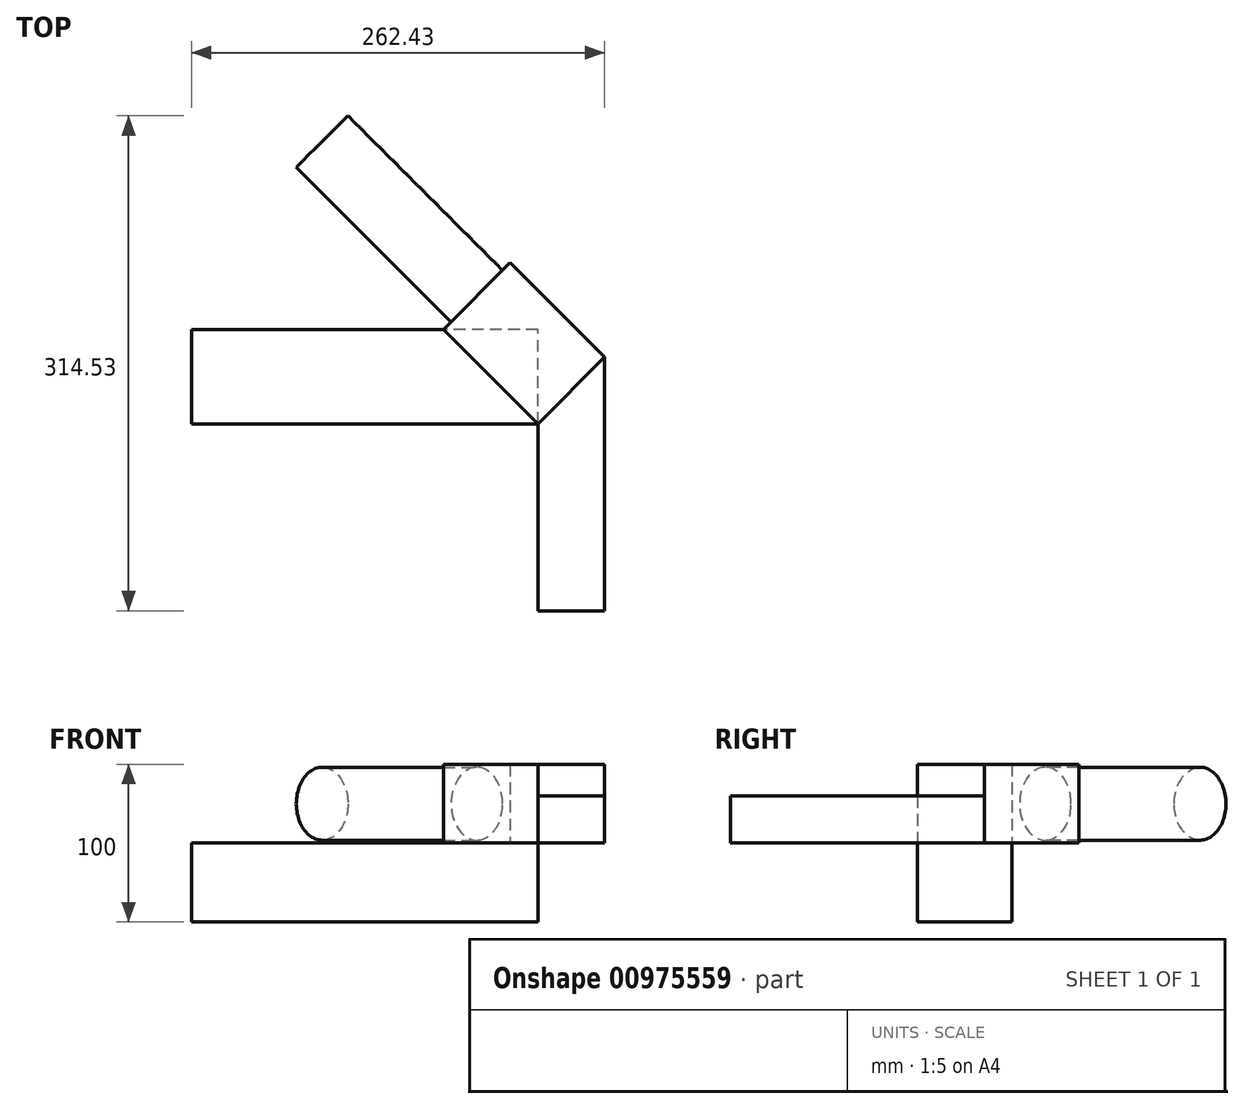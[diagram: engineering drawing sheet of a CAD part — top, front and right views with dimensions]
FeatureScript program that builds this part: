
annotation { "Feature Type Name" : "Feature", "Feature Type Description" : "" }
export const myFeature = defineFeature(function(context is Context, id is Id, definition is map)
    precondition{}
    {
        {
            var Q0;
            Q0=qCreatedBy(makeId("Top.planeOp"),FACE);
            var sketch = newSketch(context, id + "F0", { "sketchPlane" : qUnion([Q0])});
            skLineSegment(sketch, "E0.bottom", {"start": v(110, -30) * mm, "end": v(-110, -30) * mm});
            skLineSegment(sketch, "E0.top", {"start": v(110, 30) * mm, "end": v(-110, 30) * mm});
            skLineSegment(sketch, "E0.left", {"start": v(110, -30) * mm, "end": v(110, 30) * mm});
            skLineSegment(sketch, "E0.right", {"start": v(-110, -30) * mm, "end": v(-110, 30) * mm});
            skPoint(sketch, "E0.middle", {"position": v(0, 0) * mm});
            skSolve(sketch);
        }
        {
            var Q0;
            Q0 = qSketchRegion(id + "F0", true);
            extrude(context, id + "F1", {"entities" : qUnion([Q0]), "depth" : 50 * mm, "offsetDistance" : 25 * mm});
        }
        {
            var Q0;
            Q0=makeQuery(id+"F1.opExtrude","CAP_FACE",FACE,{"disambiguationData":[OSD([sQuery(id+"F0.wireOp",EDGE,"E0.bottom"),sQuery(id+"F0.wireOp",EDGE,"E0.top"),sQuery(id+"F0.wireOp",EDGE,"E0.left"),sQuery(id+"F0.wireOp",EDGE,"E0.right")])],"isStart":false});
            var sketch = newSketch(context, id + "F2", { "sketchPlane" : qUnion([Q0])});
            skLineSegment(sketch, "E1", {"start": v(110, -30) * mm, "end": v(50, 30) * mm});
            skLineSegment(sketch, "E2", {"start": v(110, -30) * mm, "end": v(152.43, 12.43) * mm});
            skLineSegment(sketch, "E3", {"start": v(152.43, 12.43) * mm, "end": v(92.43, 72.43) * mm});
            skLineSegment(sketch, "E4", {"start": v(92.43, 72.43) * mm, "end": v(50, 30) * mm});
            skSolve(sketch);
        }
        {
            var Q0;
            Q0 = qSketchRegion(id + "F2", true);
            extrude(context, id + "F3", {"entities" : qUnion([Q0]), "operationType" : NewBodyOperationType.ADD, "depth" : 50 * mm, "offsetDistance" : 25 * mm});
        }
        {
            var Q0;
            Q0 = qSketchRegion(id + "F2", true);
            extrude(context, id + "F4", {"entities" : qUnion([Q0]), "operationType" : NewBodyOperationType.ADD, "depth" : 25 * mm, "offsetDistance" : 25 * mm});
        }
        {
            var Q0;
            Q0=makeQuery(id+"F3.opExtrude","SWEPT_FACE",FACE,{"disambiguationData":[OSD([sQuery(id+"F2.wireOp",EDGE,"E4")])]});
            var sketch = newSketch(context, id + "F5", { "sketchPlane" : qUnion([Q0])});
            skPoint(sketch, "E5", {"position": v(-86.57, 75) * mm});
            skCircle(sketch, "E6", {"center": v(-86.57, 75) * mm, "radius": 20 * mm});
            skSolve(sketch);
        }
        {
            var Q0;
            Q0 = qSketchRegion(id + "F5", true);
            extrude(context, id + "F6", {"entities" : qUnion([Q0]), "operationType" : NewBodyOperationType.REMOVE, "oppositeDirection" : true, "depth" : 60 * mm, "offsetDistance" : 25 * mm, "hasDraft" : true, "draftAngle" : 3 * degree});
        }
        {
            var Q0;
            Q0=makeQuery(id+"F6.boolean.opBoolean","COPY",FACE,{"derivedFrom":makeQuery(id+"F6.opExtrude","CAP_FACE",FACE,{"disambiguationData":[OSD([sQuery(id+"F5.wireOp",EDGE,"E6")])],"isStart":false})});
            extrude(context, id + "F7", {"entities" : qUnion([Q0]), "operationType" : NewBodyOperationType.ADD, "depth" : 199 * mm, "offsetDistance" : 25 * mm});
        }
        {
            var Q0;
            Q0=makeQuery(id+"F1.opExtrude","CAP_FACE",FACE,{"disambiguationData":[OSD([sQuery(id+"F0.wireOp",EDGE,"E0.bottom"),sQuery(id+"F0.wireOp",EDGE,"E0.top"),sQuery(id+"F0.wireOp",EDGE,"E0.left"),sQuery(id+"F0.wireOp",EDGE,"E0.right")])],"isStart":false});
            var sketch = newSketch(context, id + "F8", { "sketchPlane" : qUnion([Q0])});
            skLineSegment(sketch, "E7", {"start": v(110, -30) * mm, "end": v(110, -148.66) * mm});
            skLineSegment(sketch, "E8", {"start": v(110, -148.66) * mm, "end": v(152.43, -148.66) * mm});
            skLineSegment(sketch, "E9", {"start": v(152.43, -148.66) * mm, "end": v(152.43, 12.43) * mm});
            skLineSegment(sketch, "E10", {"start": v(152.43, 12.43) * mm, "end": v(110, -30) * mm});
            skSolve(sketch);
        }
        {
            var Q0;
            Q0 = qSketchRegion(id + "F8", true);
            extrude(context, id + "F9", {"entities" : qUnion([Q0]), "operationType" : NewBodyOperationType.ADD, "depth" : 30 * mm, "offsetDistance" : 25 * mm});
        }
    });
